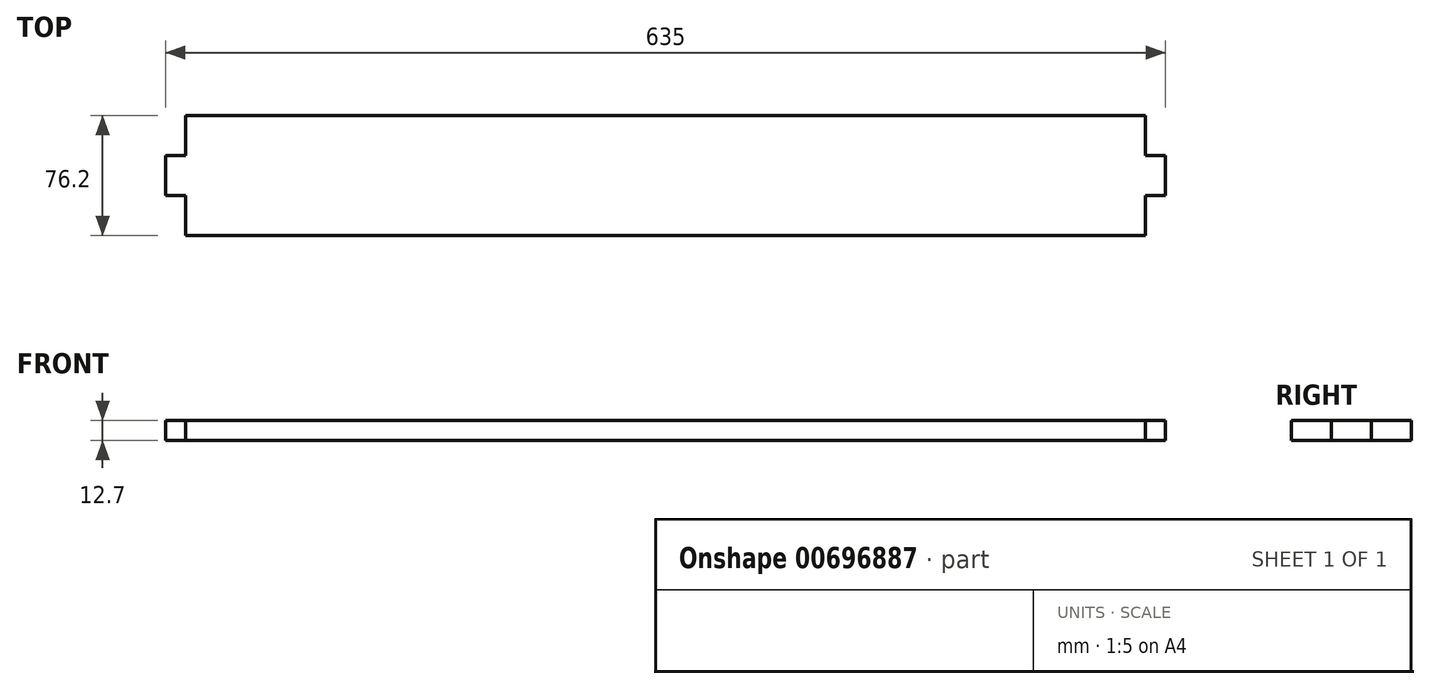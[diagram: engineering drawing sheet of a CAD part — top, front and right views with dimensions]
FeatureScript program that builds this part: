
annotation { "Feature Type Name" : "Feature", "Feature Type Description" : "" }
export const myFeature = defineFeature(function(context is Context, id is Id, definition is map)
    precondition{}
    {
        {
            var Q0;
            Q0=qCreatedBy(makeId("Top.planeOp"),FACE);
            var sketch = newSketch(context, id + "F0", { "sketchPlane" : qUnion([Q0])});
            skLineSegment(sketch, "E0.bottom", {"start": v(-191.32, -50.66) * mm, "end": v(418.28, -50.66) * mm});
            skLineSegment(sketch, "E0.top", {"start": v(-191.32, 25.54) * mm, "end": v(418.28, 25.54) * mm});
            skLineSegment(sketch, "E0.left", {"start": v(-191.32, -50.66) * mm, "end": v(-191.32, 25.54) * mm});
            skLineSegment(sketch, "E0.right", {"start": v(418.28, -50.66) * mm, "end": v(418.28, 25.54) * mm});
            skLineSegment(sketch, "E1.top", {"start": v(-191.32, 0.14) * mm, "end": v(-204.02, 0.14) * mm});
            skLineSegment(sketch, "E2.MirrorCS", {"start": v(-191.32, -25.26) * mm, "end": v(-204.02, -25.26) * mm});
            skLineSegment(sketch, "E3.MirrorCS", {"start": v(1040.58, -12.56) * mm, "end": v(1040.58, 0.14) * mm});
            skLineSegment(sketch, "E4.MirrorCS", {"start": v(1040.58, -12.56) * mm, "end": v(1040.58, -25.26) * mm});
            skLineSegment(sketch, "E5.MirrorCS", {"start": v(1027.88, 0.14) * mm, "end": v(1040.58, 0.14) * mm});
            skLineSegment(sketch, "E6.MirrorCS", {"start": v(1027.88, -25.26) * mm, "end": v(1040.58, -25.26) * mm});
            skLineSegment(sketch, "E7.bottom", {"start": v(418.28, -25.26) * mm, "end": v(430.98, -25.26) * mm});
            skLineSegment(sketch, "E7.top", {"start": v(418.28, 0.14) * mm, "end": v(430.98, 0.14) * mm});
            skLineSegment(sketch, "E7.right", {"start": v(430.98, -25.26) * mm, "end": v(430.98, 0.14) * mm});
            skLineSegment(sketch, "E8", {"start": v(-204.02, 0.14) * mm, "end": v(-204.02, -25.26) * mm});
            skSolve(sketch);
        }
        {
            var Q0;
            {var subQ3=sQuery(id+"F0.wireOp",EDGE,"E0.bottom");Q0=makeQuery(id+"F0.imprint","IMPRINT",FACE,{"disambiguationData":[TD([[makeQuery(id+"F0.imprint","IMPRINT",EDGE,{"derivedFrom":subQ3}),1.0]])]});}
            var Q1;
            {var subQ0=sQuery(id+"F0.wireOp",EDGE,"E7.bottom");Q1=makeQuery(id+"F0.imprint","IMPRINT",FACE,{"disambiguationData":[TD([[makeQuery(id+"F0.imprint","IMPRINT",EDGE,{"derivedFrom":subQ0}),1.0]])]});}
            var Q2;
            {var subQ0=sQuery(id+"F0.wireOp",EDGE,"E1.top");Q2=makeQuery(id+"F0.imprint","IMPRINT",FACE,{"disambiguationData":[TD([[makeQuery(id+"F0.imprint","IMPRINT",EDGE,{"derivedFrom":subQ0}),1.0]])]});}
            extrude(context, id + "F1", {"entities" : qUnion([Q0, Q1, Q2]), "depth" : 12.7 * mm, "offsetDistance" : 25.4 * mm});
        }
    });
